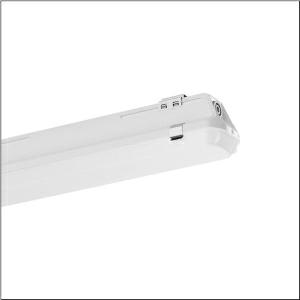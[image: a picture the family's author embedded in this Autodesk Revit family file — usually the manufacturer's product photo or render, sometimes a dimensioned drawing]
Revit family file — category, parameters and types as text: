
# Revit family: monsun_r__21_chemical_51fb30mp480b_6f39
name_source: partatom
category: Lighting Fixtures
units: mm (PartAtom-declared; Revit-internal decimal feet)

## family parameters
Cut with Voids When Loaded = No
Host = Face
Light Source = No
Part Type = Normal
Room Calculation Point = No
Round Connector Dimension = Use Diameter
Shared = No

## types (1)
- --- (1 x LED, 7750 lm, 53.6 W, 4000K)
    Apparent Load = 54 VA
    CIE Flux Codes = 48 77 93 95 100
    Color Rendering = 80
    Color Temperature = 4000K
    Default Elevation = 1800 mm
    Description = Monsun® 21 chemical, damp-proof luminaire, chain hanger, primary optical cover: enclosure, of PA, light emission: direct distribution, primary light characteristic: symmetric, installation type: suspended mounting, surface-mounted, horizontal mounting, vertical mounting, LED, rated luminous flux: 7.750lm, luminous efficacy: 145lm/W, light colour: 840, colour temperature: 4000K, control gear: ECG, with terminal, 3-pole, max. 2.5mm², mains connection: 220..240V, AC, 50/60Hz, rated input power: 54W, housing, of glass-fibre reinforced polyester, uncoated, bright grey, incl. chain hanger, length: 1.590mm, width: 90mm, height: 88mm, clip for enclosure, of stainless steel (V2A), ceiling mounting element, of stainless steel (V2A), chain hanger, of stainless steel (V2A), protection rating (complete): IP66, insulation class (complete): insulation class I (protective earthing), certification: CE, ENEC, VDE, UKCA, protection symbol: D, impact resistance: IK08, permissible operating ambient temperature: -25..+35°C, standard: EN 50419, EN 60598-2-1, corresponds to IFS (International Featured Standards) requirements for safety and quality in the food industry, for indoor or canopied outdoor use, no direct snow, no direct sun, no direct rain, contact your sales advisor before using the luminaires in applications with unclear chemical exposure, large temperature fluctuations or condensation-forming humidity, LABS conformity tested according to VDMA 24364:2018-05, packaging unit: 1 piece
    Height = 89 mm
    Lamp = 1 x LED
    Lamp Light Flux = 7750 lm
    Lamp Power = 53.6 W
    Lamp count = 1
    Length = 1590 mm
    Luminous efficacy = 145 lm/W
    Manufacturer = Siteco
    ModVariant = No
    Model = 51FB30MP480B
    Mounting Place = Ceiling
    Mounting Type = Surface mounted
    Number of Poles = 1
    OnlyDefault = Yes
    Power Factor = 1
    Product Name = Monsun® 21 chemical
    Product group = damp-proof luminaire
    ProductGroupID = 301
    Protection Class = Protection class I
    Protection Degree = IP 66
    RLX_Detail_Level = 1
    RLX_Emergency_Light_Flux = 0 lm
    RLX_Emergency_Type = 0
    RLX_Emergency_Type_DB = No
    RlxData = <blob elided: 90009 chars, md5=8b824168>
    Socket = socket
    Standby Power = 0 W
    System Light Flux = 7750 lm
    System Power = 54 W
    Type Comments = factory setting: luminous flux: 100 % | (A | C | E) | 121 mA
    Type Image = l_1006717.jpg
    URL = http://relux.com
    VarID = @adj_096951
    Voltage = 0 V
    Weight = 0.00 kg
    Width = 90 mm

## geometry (parser evidence)
native form markers: Blend x4, Sweep x12
no freeform markers — native parametric forms only
